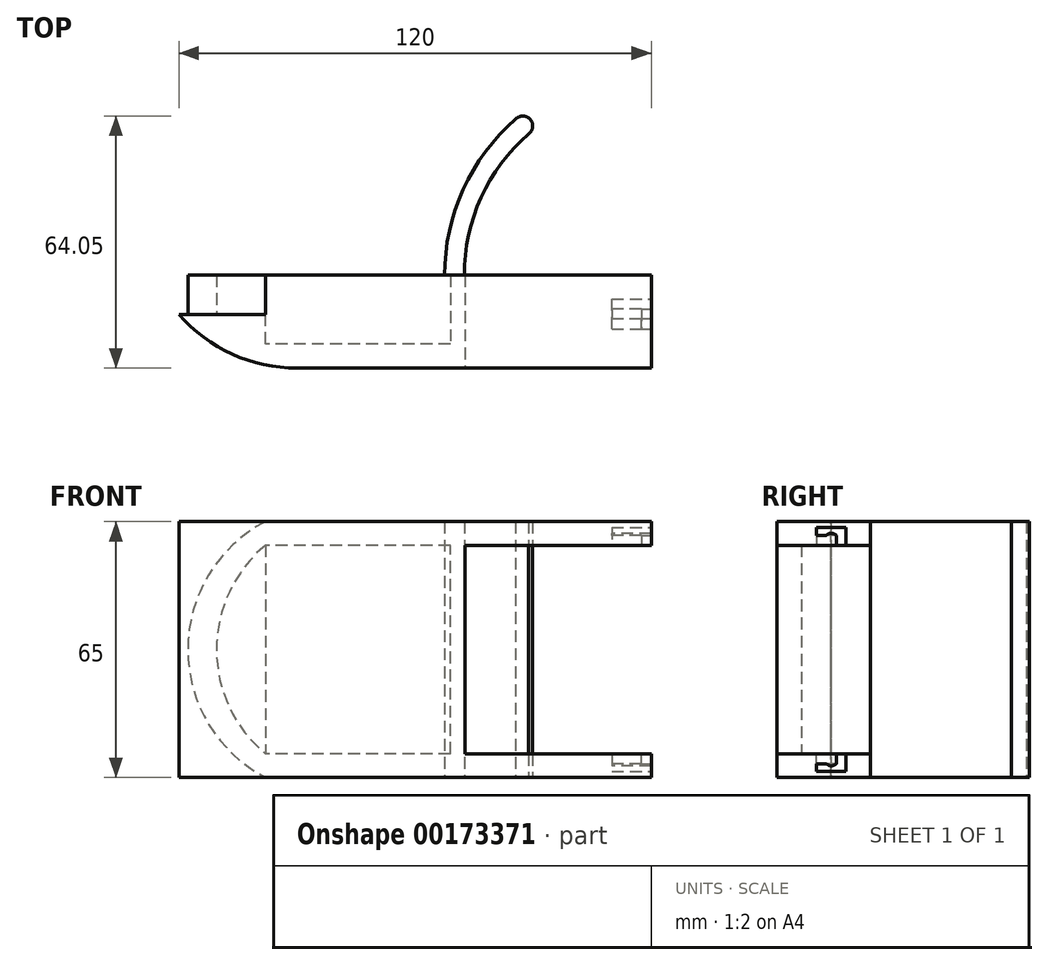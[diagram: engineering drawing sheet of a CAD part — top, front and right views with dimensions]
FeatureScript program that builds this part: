
annotation { "Feature Type Name" : "Feature", "Feature Type Description" : "" }
export const myFeature = defineFeature(function(context is Context, id is Id, definition is map)
    precondition{}
    {
        {
            var Q0;
            Q0=qCreatedBy(makeId("Top.planeOp"),FACE);
            var sketch = newSketch(context, id + "F0", { "sketchPlane" : qUnion([Q0])});
            skLineSegment(sketch, "E0.bottom", {"start": v(45, 6.82) * mm, "end": v(-45, 6.82) * mm});
            skLineSegment(sketch, "E0.top", {"start": v(45, -6.82) * mm, "end": v(-45, -6.82) * mm});
            skLineSegment(sketch, "E0.left", {"start": v(45, 6.82) * mm, "end": v(45, -6.82) * mm});
            skPoint(sketch, "E0.middle", {"position": v(0, 0) * mm});
            skLineSegment(sketch, "E1", {"start": v(-45, 6.82) * mm, "end": v(-75, 6.82) * mm});
            skArc(sketch, "E2", {"start": v(-75, 6.82) * mm, "mid": v(-61.48, -3.25) * mm, "end": v(-45, -6.82) * mm});
            skSolve(sketch);
        }
        {
            var Q0;
            Q0=makeQuery(id+"F0.imprint","IMPRINT",FACE,{"disambiguationData":[TD([[makeQuery(id+"F0.imprint","IMPRINT",EDGE,{"derivedFrom":sQuery(id+"F0.wireOp",EDGE,"E0.bottom")}),1.0]])]});
            var Q1;
            Q1 = qConstructionFilter(qBodyType(qCreatedBy(id + "F0" ,EDGE), BodyType.WIRE), ConstructionObject.NO);
            extrude(context, id + "F1", {"entities" : qUnion([Q0]), "surfaceEntities" : qUnion([Q1]), "depth" : 65 * mm});
        }
        {
            var Q0;
            Q0=makeQuery(id+"F1.opExtrude","SWEPT_FACE",FACE,{"disambiguationData":[OSD([sQuery(id+"F0.wireOp",EDGE,"E0.bottom"),sQuery(id+"F0.wireOp",EDGE,"E1")])]});
            var sketch = newSketch(context, id + "F2", { "sketchPlane" : qUnion([Q0])});
            skLineSegment(sketch, "E3.right", {"start": v(-45, 6) * mm, "end": v(-45, 59) * mm});
            skLineSegment(sketch, "E4.bottom", {"start": v(-45, 6) * mm, "end": v(0, 6) * mm});
            skLineSegment(sketch, "E4.top", {"start": v(-45, 59) * mm, "end": v(0, 59) * mm});
            skLineSegment(sketch, "E4.right", {"start": v(0, 6) * mm, "end": v(0, 59) * mm});
            skPoint(sketch, "E3.bottom.end.orphan", {"position": v(-45, 0) * mm});
            skPoint(sketch, "E5.orphan", {"position": v(-45, 65) * mm});
            skSolve(sketch);
        }
        {
            var Q0;
            Q0=makeQuery(id+"F2.imprint","IMPRINT",FACE,{"disambiguationData":[TD([[makeQuery(id+"F2.imprint","IMPRINT",EDGE,{"derivedFrom":sQuery(id+"F2.wireOp",EDGE,"E4.bottom")}),1.0]])]});
            extrude(context, id + "F3", {"entities" : qUnion([Q0]), "operationType" : NewBodyOperationType.REMOVE, "endBound" : BoundingType.THROUGH_ALL, "oppositeDirection" : true, "depth" : 25 * mm});
        }
        {
            var Q0;
            Q0=makeQuery(id+"F1.opExtrude","SWEPT_FACE",FACE,{"disambiguationData":[OSD([sQuery(id+"F0.wireOp",EDGE,"E0.bottom"),sQuery(id+"F0.wireOp",EDGE,"E1")])]});
            var sketch = newSketch(context, id + "F4", { "sketchPlane" : qUnion([Q0])});
            skLineSegment(sketch, "E6.bottom", {"start": v(0, 59) * mm, "end": v(53, 59) * mm});
            skLineSegment(sketch, "E6.top", {"start": v(0, 6) * mm, "end": v(53, 6) * mm});
            skLineSegment(sketch, "E6.left", {"start": v(0, 59) * mm, "end": v(0, 6) * mm});
            skLineSegment(sketch, "E6.right", {"start": v(53, 59) * mm, "end": v(53, 6) * mm});
            skSolve(sketch);
        }
        {
            var Q0;
            Q0=makeQuery(id+"F4.imprint","IMPRINT",FACE,{"disambiguationData":[TD([[makeQuery(id+"F4.imprint","IMPRINT",EDGE,{"derivedFrom":sQuery(id+"F4.wireOp",EDGE,"E6.bottom")}),-1.0]])]});
            extrude(context, id + "F5", {"entities" : qUnion([Q0]), "operationType" : NewBodyOperationType.REMOVE, "oppositeDirection" : true, "depth" : 7.5 * mm});
        }
        {
            var Q0;
            Q0=makeQuery(id+"F1.opExtrude","SWEPT_FACE",FACE,{"disambiguationData":[OSD([sQuery(id+"F0.wireOp",EDGE,"E0.bottom"),sQuery(id+"F0.wireOp",EDGE,"E1")])]});
            var sketch = newSketch(context, id + "F6", { "sketchPlane" : qUnion([Q0])});
            skLineSegment(sketch, "E7.bottom", {"start": v(-45, 65) * mm, "end": v(53, 65) * mm});
            skLineSegment(sketch, "E7.top", {"start": v(-45, 59) * mm, "end": v(53, 59) * mm});
            skLineSegment(sketch, "E7.left", {"start": v(-45, 65) * mm, "end": v(-45, 59) * mm});
            skLineSegment(sketch, "E8.bottom", {"start": v(-45, 6) * mm, "end": v(53, 6) * mm});
            skLineSegment(sketch, "E8.top", {"start": v(-45, 0) * mm, "end": v(53, 0) * mm});
            skLineSegment(sketch, "E8.left", {"start": v(-45, 6) * mm, "end": v(-45, 0) * mm});
            skArc(sketch, "E9", {"start": v(53, 6) * mm, "mid": v(65.44, 32.5) * mm, "end": v(53, 59) * mm});
            skArc(sketch, "E10", {"start": v(53, 0) * mm, "mid": v(72.72, 32.5) * mm, "end": v(53, 65) * mm});
            skSolve(sketch);
        }
        {
            var Q0;
            Q0=makeQuery(id+"F6.imprint","IMPRINT",FACE,{"disambiguationData":[TD([[makeQuery(id+"F6.imprint","IMPRINT",EDGE,{"derivedFrom":sQuery(id+"F6.wireOp",EDGE,"E7.bottom")}),-1.0]])]});
            extrude(context, id + "F7", {"entities" : qUnion([Q0]), "operationType" : NewBodyOperationType.ADD, "depth" : 10 * mm});
        }
        {
            var Q0;
            {var subQ1=sQuery(id+"F0.wireOp",EDGE,"E0.left");Q0=makeQuery(id+"F7.boolean.opBoolean","MERGE",FACE,{"derivedFrom":[makeQuery(id+"F3.boolean.opBoolean","SPLIT",FACE,{"disambiguationData":[TD([makeQuery(id+"F3.opExtrude","SWEPT_FACE",FACE,{"disambiguationData":[OSD([sQuery(id+"F2.wireOp",EDGE,"E4.top")])]})])],"derivedFrom":makeQuery(id+"F1.opExtrude","SWEPT_FACE",FACE,{"disambiguationData":[OSD([subQ1])]})}),makeQuery(id+"F7.opExtrude","SWEPT_FACE",FACE,{"disambiguationData":[OSD([sQuery(id+"F6.wireOp",EDGE,"E7.left")])]})]});}
            var sketch = newSketch(context, id + "F8", { "sketchPlane" : qUnion([Q0])});
            skLineSegment(sketch, "E11", {"start": v(10.68, 59) * mm, "end": v(10.68, 63.5) * mm});
            skLineSegment(sketch, "E12", {"start": v(10.68, 63.5) * mm, "end": v(3.18, 63.5) * mm});
            skLineSegment(sketch, "E13", {"start": v(3.18, 63.5) * mm, "end": v(3.18, 61.5) * mm});
            skLineSegment(sketch, "E14", {"start": v(3.18, 61.5) * mm, "end": v(8.18, 61.5) * mm});
            skLineSegment(sketch, "E15", {"start": v(8.18, 61.5) * mm, "end": v(8.18, 59) * mm});
            skLineSegment(sketch, "E16", {"start": v(10.68, 59) * mm, "end": v(8.18, 59) * mm});
            skSolve(sketch);
        }
        {
            var Q0;
            Q0=makeQuery(id+"F8.imprint","IMPRINT",FACE,{"disambiguationData":[TD([[makeQuery(id+"F8.imprint","IMPRINT",EDGE,{"derivedFrom":sQuery(id+"F8.wireOp",EDGE,"E11")}),1.0]])]});
            extrude(context, id + "F9", {"entities" : qUnion([Q0]), "operationType" : NewBodyOperationType.REMOVE, "oppositeDirection" : true, "depth" : 10 * mm});
        }
        {
            var Q0;
            Q0=makeQuery(id+"F7.boolean.opBoolean","MERGE",FACE,{"derivedFrom":[makeQuery(id+"F5.boolean.opBoolean","MERGE",FACE,{"derivedFrom":[makeQuery(id+"F3.boolean.opBoolean","COPY",FACE,{"derivedFrom":makeQuery(id+"F3.opExtrude","SWEPT_FACE",FACE,{"disambiguationData":[OSD([sQuery(id+"F2.wireOp",EDGE,"E4.top")])]})}),makeQuery(id+"F5.opExtrude","SWEPT_FACE",FACE,{"disambiguationData":[OSD([sQuery(id+"F4.wireOp",EDGE,"E6.bottom")])]})]}),makeQuery(id+"F7.opExtrude","SWEPT_FACE",FACE,{"disambiguationData":[OSD([sQuery(id+"F6.wireOp",EDGE,"E7.top")])]})]});
            var sketch = newSketch(context, id + "F10", { "sketchPlane" : qUnion([Q0])});
            skLineSegment(sketch, "E17.bottom", {"start": v(35, -8.18) * mm, "end": v(42.5, -8.18) * mm});
            skLineSegment(sketch, "E17.top", {"start": v(35, -3.18) * mm, "end": v(42.5, -3.18) * mm});
            skLineSegment(sketch, "E17.left", {"start": v(35, -8.18) * mm, "end": v(35, -3.18) * mm});
            skLineSegment(sketch, "E17.right", {"start": v(42.5, -8.18) * mm, "end": v(42.5, -3.18) * mm});
            skSolve(sketch);
        }
        {
            var Q0;
            Q0=makeQuery(id+"F10.imprint","IMPRINT",FACE,{"disambiguationData":[TD([[makeQuery(id+"F10.imprint","IMPRINT",EDGE,{"derivedFrom":sQuery(id+"F10.wireOp",EDGE,"E17.bottom")}),1.0]])]});
            extrude(context, id + "F11", {"entities" : qUnion([Q0]), "operationType" : NewBodyOperationType.REMOVE, "oppositeDirection" : true, "depth" : 3 * mm});
        }
        {
            var Q0;
            {var subQ1=sQuery(id+"F0.wireOp",EDGE,"E0.left");Q0=makeQuery(id+"F7.boolean.opBoolean","MERGE",FACE,{"derivedFrom":[makeQuery(id+"F3.boolean.opBoolean","SPLIT",FACE,{"disambiguationData":[TD([makeQuery(id+"F3.opExtrude","SWEPT_FACE",FACE,{"disambiguationData":[OSD([sQuery(id+"F2.wireOp",EDGE,"E4.bottom")])]})])],"derivedFrom":makeQuery(id+"F1.opExtrude","SWEPT_FACE",FACE,{"disambiguationData":[OSD([subQ1])]})}),makeQuery(id+"F7.opExtrude","SWEPT_FACE",FACE,{"disambiguationData":[OSD([sQuery(id+"F6.wireOp",EDGE,"E8.left")])]})]});}
            var sketch = newSketch(context, id + "F12", { "sketchPlane" : qUnion([Q0])});
            skLineSegment(sketch, "E18", {"start": v(10.68, 6) * mm, "end": v(10.68, 1.5) * mm});
            skLineSegment(sketch, "E19", {"start": v(10.68, 1.5) * mm, "end": v(3.18, 1.5) * mm});
            skLineSegment(sketch, "E20", {"start": v(3.18, 1.5) * mm, "end": v(3.18, 3.5) * mm});
            skLineSegment(sketch, "E21", {"start": v(3.18, 3.5) * mm, "end": v(8.18, 3.5) * mm});
            skLineSegment(sketch, "E22", {"start": v(8.18, 3.5) * mm, "end": v(8.18, 6) * mm});
            skLineSegment(sketch, "E23", {"start": v(8.18, 6) * mm, "end": v(10.68, 6) * mm});
            skSolve(sketch);
        }
        {
            var Q0;
            Q0=makeQuery(id+"F12.imprint","IMPRINT",FACE,{"disambiguationData":[TD([[makeQuery(id+"F12.imprint","IMPRINT",EDGE,{"derivedFrom":sQuery(id+"F12.wireOp",EDGE,"E18")}),-1.0]])]});
            extrude(context, id + "F13", {"entities" : qUnion([Q0]), "operationType" : NewBodyOperationType.REMOVE, "oppositeDirection" : true, "depth" : 10 * mm});
        }
        {
            var Q0;
            Q0=makeQuery(id+"F7.boolean.opBoolean","MERGE",FACE,{"derivedFrom":[makeQuery(id+"F5.boolean.opBoolean","MERGE",FACE,{"derivedFrom":[makeQuery(id+"F3.boolean.opBoolean","COPY",FACE,{"derivedFrom":makeQuery(id+"F3.opExtrude","SWEPT_FACE",FACE,{"disambiguationData":[OSD([sQuery(id+"F2.wireOp",EDGE,"E4.bottom")])]})}),makeQuery(id+"F5.opExtrude","SWEPT_FACE",FACE,{"disambiguationData":[OSD([sQuery(id+"F4.wireOp",EDGE,"E6.top")])]})]}),makeQuery(id+"F7.opExtrude","SWEPT_FACE",FACE,{"disambiguationData":[OSD([sQuery(id+"F6.wireOp",EDGE,"E8.bottom")])]})]});
            var sketch = newSketch(context, id + "F14", { "sketchPlane" : qUnion([Q0])});
            skLineSegment(sketch, "E24.bottom", {"start": v(35, 8.18) * mm, "end": v(42.5, 8.18) * mm});
            skLineSegment(sketch, "E24.top", {"start": v(35, 3.18) * mm, "end": v(42.5, 3.18) * mm});
            skLineSegment(sketch, "E24.left", {"start": v(35, 8.18) * mm, "end": v(35, 3.18) * mm});
            skLineSegment(sketch, "E24.right", {"start": v(42.5, 8.18) * mm, "end": v(42.5, 3.18) * mm});
            skSolve(sketch);
        }
        {
            var Q0;
            Q0=makeQuery(id+"F14.imprint","IMPRINT",FACE,{"disambiguationData":[TD([[makeQuery(id+"F14.imprint","IMPRINT",EDGE,{"derivedFrom":sQuery(id+"F14.wireOp",EDGE,"E24.bottom")}),-1.0]])]});
            extrude(context, id + "F15", {"entities" : qUnion([Q0]), "operationType" : NewBodyOperationType.REMOVE, "oppositeDirection" : true, "depth" : 3 * mm});
        }
        {
            var Q0;
            Q0=makeQuery(id+"F15.boolean.opBoolean","MERGE",FACE,{"derivedFrom":[makeQuery(id+"F13.boolean.opBoolean","COPY",FACE,{"derivedFrom":makeQuery(id+"F13.opExtrude","CAP_FACE",FACE,{"disambiguationData":[OSD([sQuery(id+"F12.wireOp",EDGE,"E18"),sQuery(id+"F12.wireOp",EDGE,"E19"),sQuery(id+"F12.wireOp",EDGE,"E20"),sQuery(id+"F12.wireOp",EDGE,"E21"),sQuery(id+"F12.wireOp",EDGE,"E22"),sQuery(id+"F12.wireOp",EDGE,"E23")])],"isStart":false})}),makeQuery(id+"F15.opExtrude","SWEPT_FACE",FACE,{"disambiguationData":[OSD([sQuery(id+"F14.wireOp",EDGE,"E24.left")])]})]});
            var sketch = newSketch(context, id + "F16", { "sketchPlane" : qUnion([Q0])});
            skArc(sketch, "E25", {"start": v(5.68, 3.5) * mm, "mid": v(6.93, 2.95) * mm, "end": v(8.18, 3.5) * mm});
            skLineSegment(sketch, "E26", {"start": v(8.18, 3.5) * mm, "end": v(5.68, 3.5) * mm});
            skSolve(sketch);
        }
        {
            var Q0;
            Q0=makeQuery(id+"F16.imprint","IMPRINT",FACE,{"disambiguationData":[TD([[makeQuery(id+"F16.imprint","IMPRINT",EDGE,{"derivedFrom":sQuery(id+"F16.wireOp",EDGE,"E25")}),1.0]])]});
            extrude(context, id + "F17", {"entities" : qUnion([Q0]), "operationType" : NewBodyOperationType.ADD, "depth" : 10 * mm});
        }
        {
            var Q0;
            Q0=makeQuery(id+"F11.boolean.opBoolean","MERGE",FACE,{"derivedFrom":[makeQuery(id+"F9.boolean.opBoolean","COPY",FACE,{"derivedFrom":makeQuery(id+"F9.opExtrude","CAP_FACE",FACE,{"disambiguationData":[OSD([sQuery(id+"F8.wireOp",EDGE,"E11"),sQuery(id+"F8.wireOp",EDGE,"E12"),sQuery(id+"F8.wireOp",EDGE,"E13"),sQuery(id+"F8.wireOp",EDGE,"E14"),sQuery(id+"F8.wireOp",EDGE,"E15"),sQuery(id+"F8.wireOp",EDGE,"E16")])],"isStart":false})}),makeQuery(id+"F11.opExtrude","SWEPT_FACE",FACE,{"disambiguationData":[OSD([sQuery(id+"F10.wireOp",EDGE,"E17.left")])]})]});
            var sketch = newSketch(context, id + "F18", { "sketchPlane" : qUnion([Q0])});
            skArc(sketch, "E27", {"start": v(8.18, 61.5) * mm, "mid": v(6.93, 62.05) * mm, "end": v(5.68, 61.5) * mm});
            skLineSegment(sketch, "E28", {"start": v(8.18, 61.5) * mm, "end": v(5.68, 61.5) * mm});
            skSolve(sketch);
        }
        {
            var Q0;
            Q0=makeQuery(id+"F18.imprint","IMPRINT",FACE,{"disambiguationData":[TD([[makeQuery(id+"F18.imprint","IMPRINT",EDGE,{"derivedFrom":sQuery(id+"F18.wireOp",EDGE,"E27")}),1.0]])]});
            extrude(context, id + "F19", {"entities" : qUnion([Q0]), "operationType" : NewBodyOperationType.ADD, "depth" : 10 * mm});
        }
        {
            var Q0;
            Q0=makeQuery(id+"F5.boolean.opBoolean","COPY",FACE,{"derivedFrom":makeQuery(id+"F5.opExtrude","CAP_FACE",FACE,{"disambiguationData":[OSD([sQuery(id+"F4.wireOp",EDGE,"E6.bottom"),sQuery(id+"F4.wireOp",EDGE,"E6.top"),sQuery(id+"F4.wireOp",EDGE,"E6.left"),sQuery(id+"F4.wireOp",EDGE,"E6.right")])],"isStart":false})});
            var sketch = newSketch(context, id + "F20", { "sketchPlane" : qUnion([Q0])});
            skLineSegment(sketch, "E29.bottom", {"start": v(6, 6) * mm, "end": v(0, 6) * mm});
            skLineSegment(sketch, "E29.top", {"start": v(6, 59) * mm, "end": v(0, 59) * mm});
            skLineSegment(sketch, "E29.left", {"start": v(6, 6) * mm, "end": v(6, 59) * mm});
            skLineSegment(sketch, "E29.right", {"start": v(0, 6) * mm, "end": v(0, 59) * mm});
            skSolve(sketch);
        }
        {
            var Q0;
            Q0=makeQuery(id+"F20.imprint","IMPRINT",FACE,{"disambiguationData":[TD([[makeQuery(id+"F20.imprint","IMPRINT",EDGE,{"derivedFrom":sQuery(id+"F20.wireOp",EDGE,"E29.bottom")}),1.0]])]});
            extrude(context, id + "F21", {"entities" : qUnion([Q0]), "operationType" : NewBodyOperationType.ADD, "depth" : 17.5 * mm});
        }
        {
            var Q0;
            Q0=makeQuery(id+"F7.boolean.opBoolean","MERGE",FACE,{"derivedFrom":[makeQuery(id+"F1.opExtrude","CAP_FACE",FACE,{"disambiguationData":[OSD([sQuery(id+"F0.wireOp",EDGE,"E0.bottom"),sQuery(id+"F0.wireOp",EDGE,"E0.top"),sQuery(id+"F0.wireOp",EDGE,"E0.left"),sQuery(id+"F0.wireOp",EDGE,"E1"),sQuery(id+"F0.wireOp",EDGE,"E2")])],"isStart":true}),makeQuery(id+"F7.opExtrude","SWEPT_FACE",FACE,{"disambiguationData":[OSD([sQuery(id+"F6.wireOp",EDGE,"E8.top")])]})]});
            var sketch = newSketch(context, id + "F22", { "sketchPlane" : qUnion([Q0])});
            skLineSegment(sketch, "E30", {"start": v(-2.5, -16.82) * mm, "end": v(-7.5, -16.82) * mm});
            skArc(sketch, "E31", {"start": v(-7.5, -16.82) * mm, "mid": v(-2.78, -38.58) * mm, "end": v(10.54, -56.43) * mm});
            skArc(sketch, "E32", {"start": v(-2.5, -16.82) * mm, "mid": v(1.77, -36.51) * mm, "end": v(13.82, -52.66) * mm});
            skArc(sketch, "E33", {"start": v(10.54, -56.43) * mm, "mid": v(14.28, -56.37) * mm, "end": v(13.82, -52.66) * mm});
            skSolve(sketch);
        }
        {
            var Q0;
            Q0=makeQuery(id+"F22.imprint","IMPRINT",FACE,{"disambiguationData":[TD([[makeQuery(id+"F22.imprint","IMPRINT",EDGE,{"derivedFrom":sQuery(id+"F22.wireOp",EDGE,"E30")}),1.0]])]});
            extrude(context, id + "F23", {"entities" : qUnion([Q0]), "oppositeDirection" : true, "depth" : 65 * mm});
        }
        {
            var Q0;
            Q0=makeQuery(id+"F1.opExtrude","SWEPT_FACE",FACE,{"disambiguationData":[OSD([sQuery(id+"F0.wireOp",EDGE,"E0.top")])]});
            var sketch = newSketch(context, id + "F24", { "sketchPlane" : qUnion([Q0])});
            skLineSegment(sketch, "E34.bottom", {"start": v(0, 6) * mm, "end": v(-2.3, 6) * mm});
            skLineSegment(sketch, "E34.top", {"start": v(0, 59) * mm, "end": v(-2.3, 59) * mm});
            skLineSegment(sketch, "E34.left", {"start": v(0, 6) * mm, "end": v(0, 59) * mm});
            skLineSegment(sketch, "E34.right", {"start": v(-2.3, 6) * mm, "end": v(-2.3, 59) * mm});
            skSolve(sketch);
        }
        {
            var Q0;
            Q0=makeQuery(id+"F24.imprint","IMPRINT",FACE,{"disambiguationData":[TD([[makeQuery(id+"F24.imprint","IMPRINT",EDGE,{"derivedFrom":sQuery(id+"F24.wireOp",EDGE,"E34.bottom")}),-1.0]])]});
            extrude(context, id + "F25", {"entities" : qUnion([Q0]), "operationType" : NewBodyOperationType.REMOVE, "oppositeDirection" : true, "depth" : 25 * mm});
        }
    });
